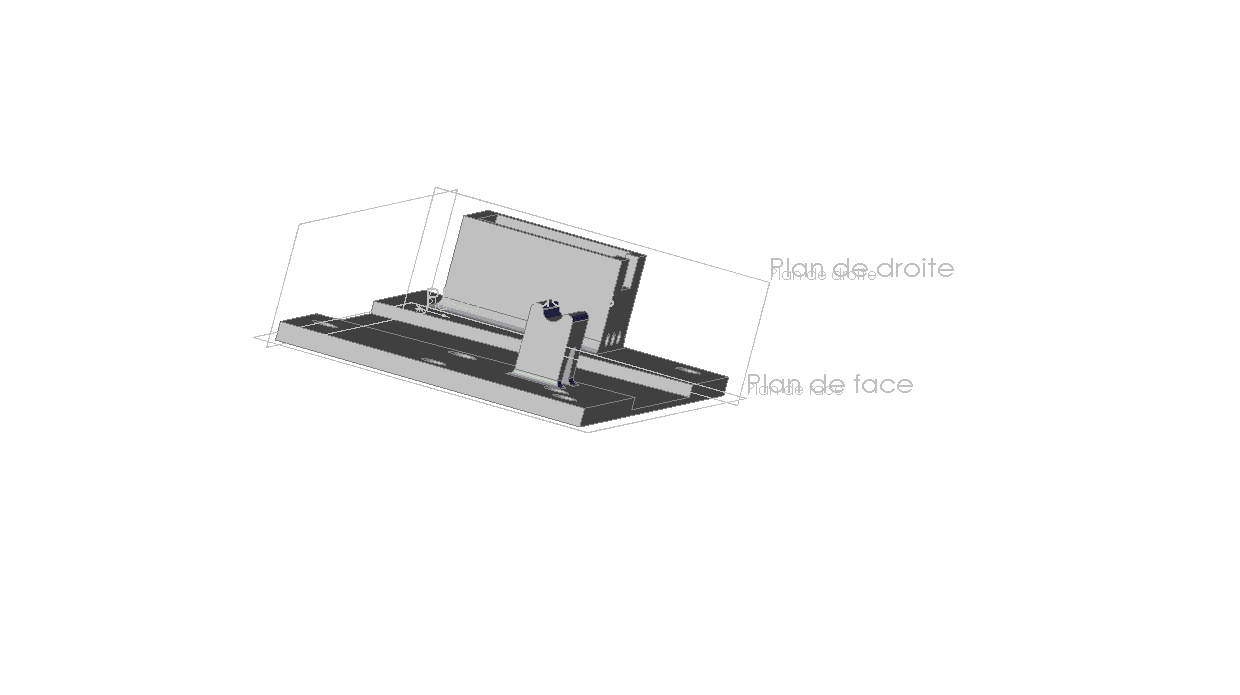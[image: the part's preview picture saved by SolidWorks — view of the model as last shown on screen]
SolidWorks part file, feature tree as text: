
SOLIDWORKS PART (.sldprt)
format: sldprt  version: not decoded by parser v0  size: 462,336 bytes
history: native  units: mm
features: sketch x12, cut_extrude x8, fillet x8, extrude x4, plane x3, material x1 (+10 scaffold rows collapsed)
feature tree (46):
  scaffold x10  (default folders/planes/origin — collapsed)
  material  "Matériau <non spécifié>"
  plane  "Plan de face"
  plane  "Plan de dessus"
  plane  "Plan de droite"
  sketch  "Esquisse1"  dims[D1=100.0mm D2=50.0mm]
  extrude  "Extrusion1"  Depth=1mm
  sketch  "Esquisse2"  dims[D1=35.0mm D2=35.0mm D3=25.0mm]
  extrude  "Extrusion2"  Depth=2mm
  sketch  "Esquisse4"  dims[D1=17.0mm D2=26.0mm]
  extrude  "Extrusion3"  Depth=15mm
  sketch  "Esquisse5"  dims[D1=2.0mm D2=2.0mm]
  cut_extrude  "Enlèv. mat.-Extru.1"  Depth=11mm
  sketch  "Esquisse6"  dims[D1=15.0mm D2=3.5mm]
  cut_extrude  "Enlèv. mat.-Extru.2"  Depth=4mm
  sketch  "Esquisse7"  dims[D1=6.0mm D2=3.5mm]
  cut_extrude  "Enlèv. mat.-Extru.3"  Depth=5mm
  sketch  "Esquisse8"  dims[D1=6.5mm D2=4.0mm D3=4.0mm]
  cut_extrude  "Enlèv. mat.-Extru.4"  Depth=8mm
  sketch  "Esquisse10"  dims[D1=7.0mm D2=5.0mm D3=5.0mm D4=7.0mm D5=38.0mm D6=14.0mm D7=14.0mm]
  cut_extrude  "Enlèv. mat.-Extru.5"  [1 undecoded]
  fillet  "Congé1"  Radius=2mm
  fillet  "Congé2"  Radius=2mm
  fillet  "Congé3"  Radius=2mm
  sketch  "Esquisse12"
  extrude  "Extrusion5"  Depth=18mm
  sketch  "Esquisse13"  dims[D1=2.0mm]
  cut_extrude  "Enlèv. mat.-Extru.8"  Depth=15mm
  fillet  "Congé6"  Radius=1mm
  fillet  "Congé7"  Radius=1mm
  sketch  "Esquisse14"  dims[D1=3.0mm D2=3.0mm D3=6.0mm]
  cut_extrude  "Enlèv. mat.-Extru.9"  [1 undecoded]
  sketch  "Esquisse15"  dims[D1=20.0mm]
  cut_extrude  "Enlèv. mat.-Extru.10"  [1 undecoded]
  fillet  "Congé8"  Radius=1mm
  fillet  "Congé9"  Radius=1mm
  fillet  "Congé10"  Radius=1mm
decode coverage: 28 of 32 modeling features carry decoded parameters
note: 3 parameter values undecoded
summary: no parameter record found for 3 features
note: suppression state not decoded; provenance and decode notes live in map.json
